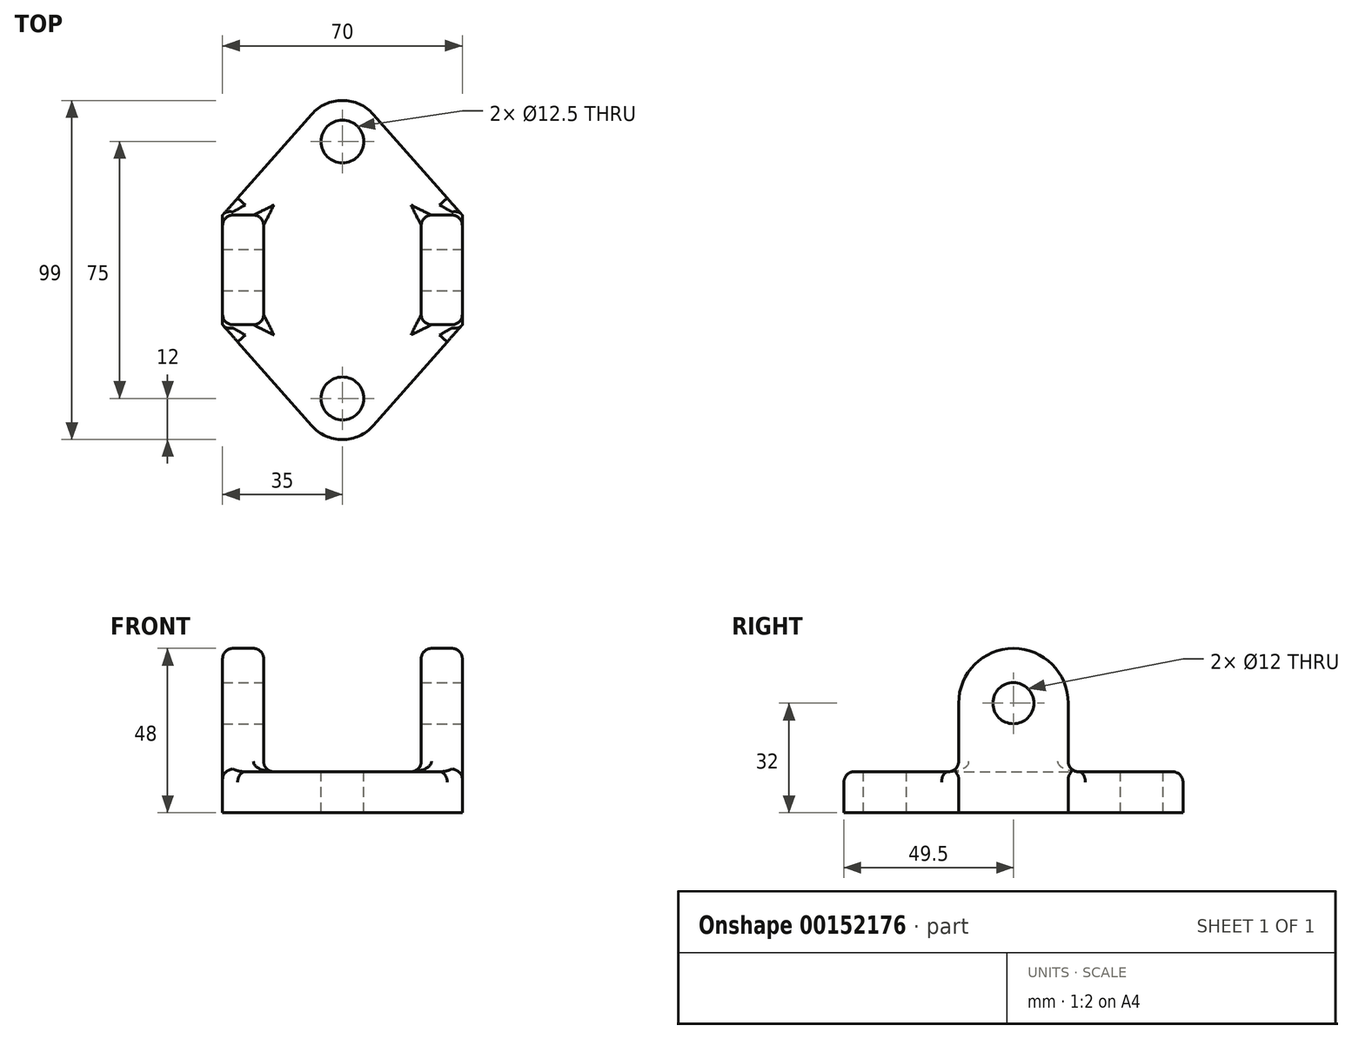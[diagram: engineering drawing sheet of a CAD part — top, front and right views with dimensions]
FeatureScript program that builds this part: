
annotation { "Feature Type Name" : "Feature", "Feature Type Description" : "" }
export const myFeature = defineFeature(function(context is Context, id is Id, definition is map)
    precondition{}
    {
        {
            var Q0;
            Q0=qCreatedBy(makeId("Right.planeOp"),FACE);
            var sketch = newSketch(context, id + "F0", { "sketchPlane" : qUnion([Q0])});
            skLineSegment(sketch, "E0.bottom", {"start": v(-16, 0) * mm, "end": v(16, 0) * mm});
            skLineSegment(sketch, "E0.left", {"start": v(-16, 0) * mm, "end": v(-16, 32) * mm});
            skLineSegment(sketch, "E0.right", {"start": v(16, 0) * mm, "end": v(16, 32) * mm});
            skArc(sketch, "E1", {"start": v(16, 32) * mm, "mid": v(0, 48) * mm, "end": v(-16, 32) * mm});
            skCircle(sketch, "E2", {"center": v(0, 32) * mm, "radius": 6 * mm});
            skSolve(sketch);
        }
        {
            var Q0;
            Q0=qSketchRegion(id+"F0",true);
            extrude(context, id + "F1", {"entities" : qUnion([Q0]), "oppositeDirection" : true, "depth" : 12 * mm});
        }
        {
            var Q0;
            Q0=qCreatedBy(makeId("Top.planeOp"),FACE);
            var sketch = newSketch(context, id + "F2", { "sketchPlane" : qUnion([Q0])});
            skLineSegment(sketch, "E3", {"start": v(-12, 16) * mm, "end": v(14, 45.44) * mm});
            skLineSegment(sketch, "E4", {"start": v(-12, -16) * mm, "end": v(14, -45.44) * mm});
            skLineSegment(sketch, "E5", {"start": v(32, -45.44) * mm, "end": v(58, -16) * mm});
            skLineSegment(sketch, "E6", {"start": v(58, -16) * mm, "end": v(58, 16) * mm});
            skLineSegment(sketch, "E7", {"start": v(58, 16) * mm, "end": v(32, 45.44) * mm});
            skArc(sketch, "E8", {"start": v(32, 45.44) * mm, "mid": v(23, 49.5) * mm, "end": v(14, 45.44) * mm});
            skArc(sketch, "E9", {"start": v(14, -45.44) * mm, "mid": v(23, -49.5) * mm, "end": v(32, -45.44) * mm});
            skLineSegment(sketch, "E10", {"start": v(23, 37.5) * mm, "end": v(23, -37.5) * mm, "construction": true});
            skLineSegment(sketch, "E11", {"start": v(-12, 0) * mm, "end": v(58, 0) * mm, "construction": true});
            skLineSegment(sketch, "E12", {"start": v(-12, 16) * mm, "end": v(58, 16) * mm, "construction": true});
            skLineSegment(sketch, "E13", {"start": v(58, -16) * mm, "end": v(-12, -16) * mm, "construction": true});
            skLineSegment(sketch, "E14", {"start": v(-12, 16) * mm, "end": v(-12, -16) * mm});
            skSolve(sketch);
        }
        {
            var Q0;
            Q0=qSketchRegion(id+"F2",true);
            extrude(context, id + "F3", {"entities" : qUnion([Q0]), "operationType" : NewBodyOperationType.ADD, "depth" : 12 * mm});
        }
        {
            var Q0;
            Q0=makeQuery(id+"F3.opExtrude","SWEPT_FACE",FACE,{"disambiguationData":[OSD([sQuery(id+"F2.wireOp",EDGE,"E6")])]});
            var sketch = newSketch(context, id + "F4", { "sketchPlane" : qUnion([Q0])});
            skCircle(sketch, "E15.0", {"center": v(0, 32) * mm, "radius": 6 * mm});
            skArc(sketch, "E16.0", {"start": v(16, 32) * mm, "mid": v(0, 48) * mm, "end": v(-16, 32) * mm});
            skLineSegment(sketch, "E17.0", {"start": v(-16, 12) * mm, "end": v(-16, 32) * mm});
            skLineSegment(sketch, "E18.0", {"start": v(-16, 0) * mm, "end": v(16, 0) * mm});
            skLineSegment(sketch, "E19.0", {"start": v(16, 12) * mm, "end": v(16, 32) * mm});
            skLineSegment(sketch, "E20.0", {"start": v(-16, 0) * mm, "end": v(-16, 12) * mm});
            skLineSegment(sketch, "E21.0", {"start": v(16, 0) * mm, "end": v(16, 12) * mm});
            skSolve(sketch);
        }
        {
            var Q0;
            Q0=qSketchRegion(id+"F4",true);
            extrude(context, id + "F5", {"entities" : qUnion([Q0]), "operationType" : NewBodyOperationType.ADD, "oppositeDirection" : true, "depth" : 12 * mm});
        }
        {
            var Q0;
            Q0=makeQuery(id+"F3.opExtrude","CAP_FACE",FACE,{"disambiguationData":[OSD([sQuery(id+"F2.wireOp",EDGE,"E3"),sQuery(id+"F2.wireOp",EDGE,"E4"),sQuery(id+"F2.wireOp",EDGE,"E5"),sQuery(id+"F2.wireOp",EDGE,"E6"),sQuery(id+"F2.wireOp",EDGE,"E7"),sQuery(id+"F2.wireOp",EDGE,"E8"),sQuery(id+"F2.wireOp",EDGE,"E9"),sQuery(id+"F2.wireOp",EDGE,"E14")])],"isStart":false});
            var sketch = newSketch(context, id + "F6", { "sketchPlane" : qUnion([Q0])});
            skCircle(sketch, "E22", {"center": v(23, 37.5) * mm, "radius": 6.25 * mm});
            skCircle(sketch, "E23", {"center": v(23, -37.5) * mm, "radius": 6.25 * mm});
            skSolve(sketch);
        }
        {
            var Q0;
            Q0=qSketchRegion(id+"F6",true);
            extrude(context, id + "F7", {"entities" : qUnion([Q0]), "operationType" : NewBodyOperationType.REMOVE, "oppositeDirection" : true, "depth" : 12 * mm});
        }
        {
            var Q0;
            Q0=makeQuery(id+"F3.boolean.opBoolean","INTERSECT",EDGE,{"derivedFrom":[makeQuery(id+"F1.opExtrude","SWEPT_FACE",FACE,{"disambiguationData":[OSD([sQuery(id+"F0.wireOp",EDGE,"E0.left")])]}),makeQuery(id+"F3.opExtrude","CAP_FACE",FACE,{"disambiguationData":[OSD([sQuery(id+"F2.wireOp",EDGE,"E3"),sQuery(id+"F2.wireOp",EDGE,"E4"),sQuery(id+"F2.wireOp",EDGE,"E5"),sQuery(id+"F2.wireOp",EDGE,"E6"),sQuery(id+"F2.wireOp",EDGE,"E7"),sQuery(id+"F2.wireOp",EDGE,"E8"),sQuery(id+"F2.wireOp",EDGE,"E9"),sQuery(id+"F2.wireOp",EDGE,"E14")])],"isStart":false})]});
            var Q1;
            Q1=makeQuery(id+"F5.boolean.opBoolean","INTERSECT",EDGE,{"derivedFrom":[makeQuery(id+"F3.opExtrude","CAP_FACE",FACE,{"disambiguationData":[OSD([sQuery(id+"F2.wireOp",EDGE,"E3"),sQuery(id+"F2.wireOp",EDGE,"E4"),sQuery(id+"F2.wireOp",EDGE,"E5"),sQuery(id+"F2.wireOp",EDGE,"E6"),sQuery(id+"F2.wireOp",EDGE,"E7"),sQuery(id+"F2.wireOp",EDGE,"E8"),sQuery(id+"F2.wireOp",EDGE,"E9"),sQuery(id+"F2.wireOp",EDGE,"E14")])],"isStart":false}),makeQuery(id+"F5.opExtrude","SWEPT_FACE",FACE,{"disambiguationData":[OSD([sQuery(id+"F4.wireOp",EDGE,"E17.0"),sQuery(id+"F4.wireOp",EDGE,"E20.0")])]})]});
            var Q2;
            Q2=makeQuery(id+"F5.boolean.opBoolean","INTERSECT",EDGE,{"derivedFrom":[makeQuery(id+"F3.opExtrude","CAP_FACE",FACE,{"disambiguationData":[OSD([sQuery(id+"F2.wireOp",EDGE,"E3"),sQuery(id+"F2.wireOp",EDGE,"E4"),sQuery(id+"F2.wireOp",EDGE,"E5"),sQuery(id+"F2.wireOp",EDGE,"E6"),sQuery(id+"F2.wireOp",EDGE,"E7"),sQuery(id+"F2.wireOp",EDGE,"E8"),sQuery(id+"F2.wireOp",EDGE,"E9"),sQuery(id+"F2.wireOp",EDGE,"E14")])],"isStart":false}),makeQuery(id+"F5.opExtrude","CAP_FACE",FACE,{"disambiguationData":[OSD([sQuery(id+"F4.wireOp",EDGE,"E15.0"),sQuery(id+"F4.wireOp",EDGE,"E16.0"),sQuery(id+"F4.wireOp",EDGE,"E17.0"),sQuery(id+"F4.wireOp",EDGE,"E18.0"),sQuery(id+"F4.wireOp",EDGE,"E19.0"),sQuery(id+"F4.wireOp",EDGE,"E20.0"),sQuery(id+"F4.wireOp",EDGE,"E21.0")])],"isStart":false})]});
            var Q3;
            Q3=makeQuery(id+"F3.boolean.opBoolean","INTERSECT",EDGE,{"derivedFrom":[makeQuery(id+"F1.opExtrude","CAP_FACE",FACE,{"disambiguationData":[OSD([sQuery(id+"F0.wireOp",EDGE,"E0.bottom"),sQuery(id+"F0.wireOp",EDGE,"E0.left"),sQuery(id+"F0.wireOp",EDGE,"E0.right"),sQuery(id+"F0.wireOp",EDGE,"E1"),sQuery(id+"F0.wireOp",EDGE,"E2")])],"isStart":true}),makeQuery(id+"F3.opExtrude","CAP_FACE",FACE,{"disambiguationData":[OSD([sQuery(id+"F2.wireOp",EDGE,"E3"),sQuery(id+"F2.wireOp",EDGE,"E4"),sQuery(id+"F2.wireOp",EDGE,"E5"),sQuery(id+"F2.wireOp",EDGE,"E6"),sQuery(id+"F2.wireOp",EDGE,"E7"),sQuery(id+"F2.wireOp",EDGE,"E8"),sQuery(id+"F2.wireOp",EDGE,"E9"),sQuery(id+"F2.wireOp",EDGE,"E14")])],"isStart":false})]});
            var Q4;
            Q4=makeQuery(id+"F3.boolean.opBoolean","INTERSECT",EDGE,{"derivedFrom":[makeQuery(id+"F1.opExtrude","SWEPT_FACE",FACE,{"disambiguationData":[OSD([sQuery(id+"F0.wireOp",EDGE,"E0.right")])]}),makeQuery(id+"F3.opExtrude","CAP_FACE",FACE,{"disambiguationData":[OSD([sQuery(id+"F2.wireOp",EDGE,"E3"),sQuery(id+"F2.wireOp",EDGE,"E4"),sQuery(id+"F2.wireOp",EDGE,"E5"),sQuery(id+"F2.wireOp",EDGE,"E6"),sQuery(id+"F2.wireOp",EDGE,"E7"),sQuery(id+"F2.wireOp",EDGE,"E8"),sQuery(id+"F2.wireOp",EDGE,"E9"),sQuery(id+"F2.wireOp",EDGE,"E14")])],"isStart":false})]});
            var Q5;
            Q5=makeQuery(id+"F5.boolean.opBoolean","INTERSECT",EDGE,{"derivedFrom":[makeQuery(id+"F3.opExtrude","CAP_FACE",FACE,{"disambiguationData":[OSD([sQuery(id+"F2.wireOp",EDGE,"E3"),sQuery(id+"F2.wireOp",EDGE,"E4"),sQuery(id+"F2.wireOp",EDGE,"E5"),sQuery(id+"F2.wireOp",EDGE,"E6"),sQuery(id+"F2.wireOp",EDGE,"E7"),sQuery(id+"F2.wireOp",EDGE,"E8"),sQuery(id+"F2.wireOp",EDGE,"E9"),sQuery(id+"F2.wireOp",EDGE,"E14")])],"isStart":false}),makeQuery(id+"F5.opExtrude","SWEPT_FACE",FACE,{"disambiguationData":[OSD([sQuery(id+"F4.wireOp",EDGE,"E19.0"),sQuery(id+"F4.wireOp",EDGE,"E21.0")])]})]});
            fillet(context, id + "F8", {"entities" : qUnion([Q0, Q1, Q2, Q3, Q4, Q5]), "radius" : 3 * mm, "tangentPropagation" : true, "allowEdgeOverflow" : false});
        }
        {
            var Q0;
            Q0=makeQuery(id+"F1.opExtrude","CAP_EDGE",EDGE,{"disambiguationData":[OSD([sQuery(id+"F0.wireOp",EDGE,"E1")])],"isStart":true});
            var Q1;
            Q1=makeQuery(id+"F5.opExtrude","CAP_EDGE",EDGE,{"disambiguationData":[OSD([sQuery(id+"F4.wireOp",EDGE,"E16.0")])],"isStart":false});
            var Q2;
            Q2=makeQuery(id+"F3.opExtrude","CAP_EDGE",EDGE,{"disambiguationData":[OSD([sQuery(id+"F2.wireOp",EDGE,"E3")])],"isStart":false});
            var Q3;
            Q3=makeQuery(id+"F3.opExtrude","CAP_EDGE",EDGE,{"disambiguationData":[OSD([sQuery(id+"F2.wireOp",EDGE,"E4")])],"isStart":false});
            fillet(context, id + "F9", {"entities" : qUnion([Q0, Q1, Q2, Q3]), "radius" : 3 * mm, "tangentPropagation" : true, "allowEdgeOverflow" : false});
        }
    });
